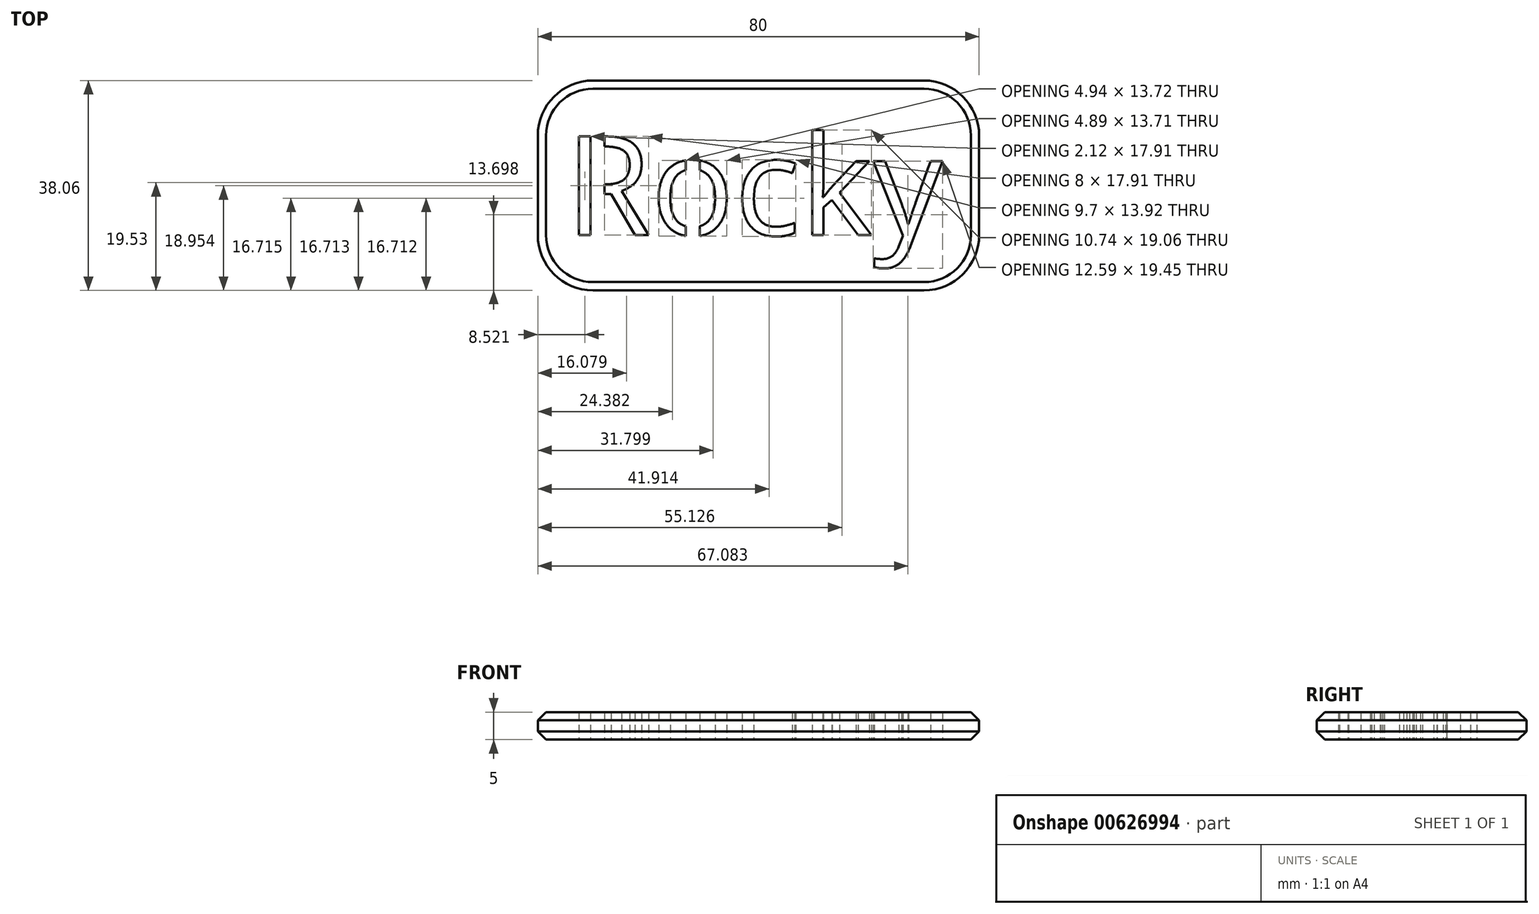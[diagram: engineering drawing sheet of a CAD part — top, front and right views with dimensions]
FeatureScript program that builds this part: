
annotation { "Feature Type Name" : "Feature", "Feature Type Description" : "" }
export const myFeature = defineFeature(function(context is Context, id is Id, definition is map)
    precondition{}
    {
        {
            var Q0;
            Q0=qCreatedBy(makeId("Top.planeOp"),FACE);
            var sketch = newSketch(context, id + "F0", { "sketchPlane" : qUnion([Q0])});
            skLineSegment(sketch, "E0.bottom", {"start": v(-35.01, 4.09) * mm, "end": v(44.99, 4.09) * mm});
            skLineSegment(sketch, "E0.top", {"start": v(-35.01, -33.97) * mm, "end": v(44.99, -33.97) * mm});
            skLineSegment(sketch, "E0.left", {"start": v(-35.01, 4.09) * mm, "end": v(-35.01, -33.97) * mm});
            skLineSegment(sketch, "E0.right", {"start": v(44.99, 4.09) * mm, "end": v(44.99, -33.97) * mm});
            skText(sketch, "E1", { "text": "Rocky\n", "fontName": "OpenSans-Regular.ttf"});
            skLineSegment(sketch, "E2.bottom", {"start": v(-8.16, -8.64) * mm, "end": v(-5.66, -8.64) * mm});
            skLineSegment(sketch, "E2.top", {"start": v(-8.16, -26.34) * mm, "end": v(-5.66, -26.34) * mm});
            skLineSegment(sketch, "E2.left", {"start": v(-8.16, -8.64) * mm, "end": v(-8.16, -26.34) * mm});
            skLineSegment(sketch, "E2.right", {"start": v(-5.66, -8.64) * mm, "end": v(-5.66, -26.34) * mm});
            skLineSegment(sketch, "E3.bottom", {"start": v(-25.43, -4.78) * mm, "end": v(-22.93, -4.78) * mm});
            skLineSegment(sketch, "E3.top", {"start": v(-25.43, -19.55) * mm, "end": v(-22.93, -19.55) * mm});
            skLineSegment(sketch, "E3.left", {"start": v(-25.43, -4.78) * mm, "end": v(-25.43, -19.55) * mm});
            skLineSegment(sketch, "E3.right", {"start": v(-22.93, -4.78) * mm, "end": v(-22.93, -19.55) * mm});
            const initialGuessF0  = {"E1": [-0.03001, -0.02397, 1, 0, 0.01806]};
            skSetInitialGuess(sketch, initialGuessF0);
            skSolve(sketch);
        }
        {
            var Q0;
            Q0 = qSketchRegion(id + "F0", true);
            var Q1;
            {var subQ5=sQuery(id+"F0.wireOp",EDGE,"E3.top");Q1=makeQuery(id+"F0.imprint","IMPRINT",FACE,{"disambiguationData":[TD([[makeQuery(id+"F0.imprint","IMPRINT",EDGE,{"derivedFrom":subQ5}),1.0]])]});}
            var Q2;
            {var subQ0=sQuery(id+"F0.wireOp",EDGE,"E3.right");var subQ1=sQuery(id+"F0.wireOp",EDGE,"E1.sketch_text.stroke-10");var subQ2=makeQuery(id+"F0.imprint","INTERSECT",VERTEX,{"derivedFrom":[subQ1,subQ0]});Q2=makeQuery(id+"F0.imprint","IMPRINT",FACE,{"disambiguationData":[TD([[makeQuery(id+"F0.imprint","IMPRINT",EDGE,{"disambiguationData":[TD([[subQ2,-1.0]])],"derivedFrom":subQ1}),-1.0]])]});}
            var Q3;
            {var subQ0=sQuery(id+"F0.wireOp",EDGE,"E3.left");var subQ1=sQuery(id+"F0.wireOp",EDGE,"E1.sketch_text.stroke-11");var subQ2=makeQuery(id+"F0.imprint","INTERSECT",VERTEX,{"derivedFrom":[subQ1,subQ0]});Q3=makeQuery(id+"F0.imprint","IMPRINT",FACE,{"disambiguationData":[TD([[makeQuery(id+"F0.imprint","IMPRINT",EDGE,{"disambiguationData":[TD([[subQ2,-1.0]])],"derivedFrom":subQ1}),1.0]])]});}
            var Q4;
            {var subQ5=sQuery(id+"F0.wireOp",EDGE,"E1.sketch_text.stroke-12");Q4=makeQuery(id+"F0.imprint","IMPRINT",FACE,{"disambiguationData":[TD([[makeQuery(id+"F0.imprint","IMPRINT",EDGE,{"derivedFrom":subQ5}),1.0]])]});}
            var Q5;
            {var subQ0=sQuery(id+"F0.wireOp",EDGE,"E3.left");var subQ1=sQuery(id+"F0.wireOp",EDGE,"E1.sketch_text.stroke-3");var subQ2=makeQuery(id+"F0.imprint","INTERSECT",VERTEX,{"derivedFrom":[subQ1,subQ0]});Q5=makeQuery(id+"F0.imprint","IMPRINT",FACE,{"disambiguationData":[TD([[makeQuery(id+"F0.imprint","IMPRINT",EDGE,{"disambiguationData":[TD([[subQ2,-1.0]])],"derivedFrom":subQ1}),-1.0]])]});}
            var Q6;
            {var subQ5=sQuery(id+"F0.wireOp",EDGE,"E3.bottom");Q6=makeQuery(id+"F0.imprint","IMPRINT",FACE,{"disambiguationData":[TD([[makeQuery(id+"F0.imprint","IMPRINT",EDGE,{"derivedFrom":subQ5}),-1.0]])]});}
            var Q7;
            {var subQ1=sQuery(id+"F0.wireOp",EDGE,"E1.sketch_text.stroke-27");Q7=makeQuery(id+"F0.imprint","IMPRINT",FACE,{"disambiguationData":[TD([[makeQuery(id+"F0.imprint","IMPRINT",EDGE,{"derivedFrom":subQ1}),1.0]])]});}
            var Q8;
            {var subQ7=sQuery(id+"F0.wireOp",EDGE,"E1.sketch_text.stroke-29");var subQ8=sQuery(id+"F0.wireOp",EDGE,"E1.sketch_text.stroke-28");var subQ9=makeQuery(id+"F0.imprint","INTERSECT",VERTEX,{"derivedFrom":[subQ8,subQ7]});Q8=makeQuery(id+"F0.imprint","IMPRINT",FACE,{"disambiguationData":[TD([[makeQuery(id+"F0.imprint","IMPRINT",EDGE,{"disambiguationData":[TD([[subQ9,1.0]])],"derivedFrom":subQ8}),1.0]])]});}
            var Q9;
            {var subQ4=sQuery(id+"F0.wireOp",EDGE,"E1.sketch_text.stroke-30");Q9=makeQuery(id+"F0.imprint","IMPRINT",FACE,{"disambiguationData":[TD([[makeQuery(id+"F0.imprint","IMPRINT",EDGE,{"derivedFrom":subQ4}),1.0]])]});}
            var Q10;
            {var subQ7=sQuery(id+"F0.wireOp",EDGE,"E1.sketch_text.stroke-25");var subQ8=sQuery(id+"F0.wireOp",EDGE,"E1.sketch_text.stroke-24");var subQ9=makeQuery(id+"F0.imprint","INTERSECT",VERTEX,{"derivedFrom":[subQ8,subQ7]});Q10=makeQuery(id+"F0.imprint","IMPRINT",FACE,{"disambiguationData":[TD([[makeQuery(id+"F0.imprint","IMPRINT",EDGE,{"disambiguationData":[TD([[subQ9,1.0]])],"derivedFrom":subQ8}),-1.0]])]});}
            var Q11;
            {var subQ1=sQuery(id+"F0.wireOp",EDGE,"E2.bottom");Q11=makeQuery(id+"F0.imprint","IMPRINT",FACE,{"disambiguationData":[TD([[makeQuery(id+"F0.imprint","IMPRINT",EDGE,{"derivedFrom":subQ1}),-1.0]])]});}
            var Q12;
            {var subQ5=sQuery(id+"F0.wireOp",EDGE,"E2.top");Q12=makeQuery(id+"F0.imprint","IMPRINT",FACE,{"disambiguationData":[TD([[makeQuery(id+"F0.imprint","IMPRINT",EDGE,{"derivedFrom":subQ5}),1.0]])]});}
            var Q13;
            {var subQ7=sQuery(id+"F0.wireOp",EDGE,"E1.sketch_text.stroke-19");var subQ9=sQuery(id+"F0.wireOp",EDGE,"E1.sketch_text.stroke-20");var subQ10=makeQuery(id+"F0.imprint","INTERSECT",VERTEX,{"derivedFrom":[subQ7,subQ9]});Q13=makeQuery(id+"F0.imprint","IMPRINT",FACE,{"disambiguationData":[TD([[makeQuery(id+"F0.imprint","IMPRINT",EDGE,{"disambiguationData":[TD([[subQ10,1.0]])],"derivedFrom":subQ7}),-1.0]])]});}
            extrude(context, id + "F1", {"entities" : qUnion([Q0, Q1, Q2, Q3, Q4, Q5, Q6, Q7, Q8, Q9, Q10, Q11, Q12, Q13]), "depth" : 5 * mm, "offsetDistance" : 25 * mm});
        }
        {
            var Q0;
            Q0=makeQuery(id+"F1.opExtrude","SWEPT_EDGE",EDGE,{"disambiguationData":[OSD([sQuery(id+"F0.wireOp",EDGE,"E0.bottom"),sQuery(id+"F0.wireOp",EDGE,"E0.left")])]});
            var Q1;
            Q1=makeQuery(id+"F1.opExtrude","SWEPT_EDGE",EDGE,{"disambiguationData":[OSD([sQuery(id+"F0.wireOp",EDGE,"E0.top"),sQuery(id+"F0.wireOp",EDGE,"E0.left")])]});
            var Q2;
            Q2=makeQuery(id+"F1.opExtrude","SWEPT_EDGE",EDGE,{"disambiguationData":[OSD([sQuery(id+"F0.wireOp",EDGE,"E0.bottom"),sQuery(id+"F0.wireOp",EDGE,"E0.right")])]});
            var Q3;
            Q3=makeQuery(id+"F1.opExtrude","SWEPT_EDGE",EDGE,{"disambiguationData":[OSD([sQuery(id+"F0.wireOp",EDGE,"E0.top"),sQuery(id+"F0.wireOp",EDGE,"E0.right")])]});
            fillet(context, id + "F2", {"entities" : qUnion([Q0, Q1, Q2, Q3]), "radius" : 10 * mm, "tangentPropagation" : true, "allowEdgeOverflow" : false});
        }
        {
            var Q0;
            Q0=makeQuery(id+"F1.opExtrude","CAP_EDGE",EDGE,{"disambiguationData":[OSD([sQuery(id+"F0.wireOp",EDGE,"E0.left")])],"isStart":false});
            var Q1;
            Q1=makeQuery(id+"F1.opExtrude","CAP_EDGE",EDGE,{"disambiguationData":[OSD([sQuery(id+"F0.wireOp",EDGE,"E0.left")])],"isStart":true});
            chamfer(context, id + "F3", {"entities" : qUnion([Q0, Q1]), "width" : 1.5 * mm, "tangentPropagation" : true});
        }
    });
